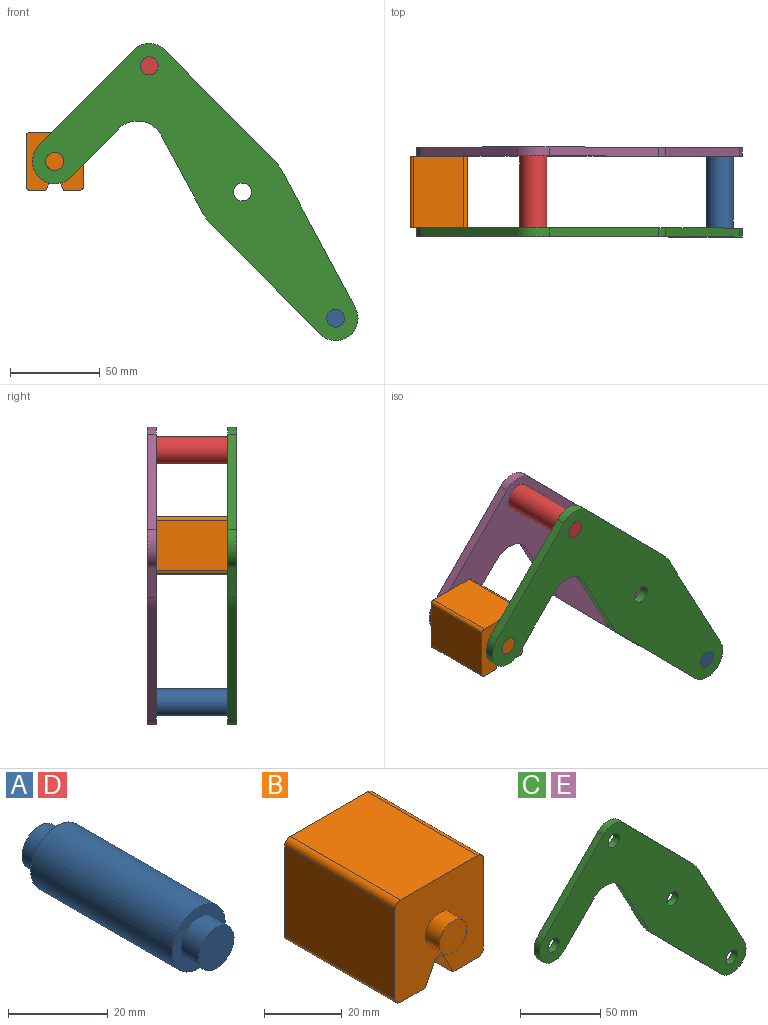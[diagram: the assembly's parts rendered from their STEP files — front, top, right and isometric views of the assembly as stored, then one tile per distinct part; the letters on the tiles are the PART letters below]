
ASSEMBLY  parts=5 mates=3
PART A: 7 faces, bbox 15x50x15 mm
  f0: cylinder r=7.5mm len=40mm, axis (0,-1,0), area 1885mm2, adj f2,f5
  f1: cylinder r=5mm len=10mm, axis (0,1,0), area 157.1mm2, adj f2,f3
  f2: plane 15x15mm, normal (0,-1,0), area 98.2mm2, adj f0,f1
  f3: plane 10x10mm, normal (0,-1,0), area 78.5mm2, adj f1
  f4: cylinder r=5mm len=10mm, axis (0,-1,0), area 157.1mm2, adj f5,f6
  f5: plane 15x15mm, normal (0,1,0), area 98.2mm2, adj f0,f4
  f6: plane 10x10mm, normal (0,1,0), area 78.5mm2, adj f4
PART B: 18 faces, bbox 32.1x50x32.1 mm
  f0: plane 40x28.08mm, normal (1,0,0), area 1123.1mm2, adj f4,f10,f13,f14
  f1: plane 40x9.04mm, normal (0,0,-1), area 361.6mm2, adj f2,f4,f10,f14
  f2: plane 40x6.42mm, normal (-0.89,0,-0.45), area 287.2mm2, adj f1,f4,f10,f15
  f3: plane 40x6.42mm, normal (0.89,0,-0.45), area 287.2mm2, adj f4,f5,f10,f15
  f4: plane 32.08x32.08mm, normal (0,-1,0), area 900.6mm2, adj f0,f1,f2,f3,f5,f6,f7,f9
  f5: plane 40x9.04mm, normal (0,0,-1), area 361.6mm2, adj f3,f4,f10,f16
  f6: plane 40x28.08mm, normal (0,0,1), area 1123.1mm2, adj f4,f10,f13,f17
  f7: plane 40x28.08mm, normal (-1,0,0), area 1123.1mm2, adj f4,f10,f16,f17
  f8: plane 10x10mm, normal (0,-1,0), area 78.5mm2, adj f9
  f9: cylinder r=5mm len=10mm, axis (0,1,0), area 157.1mm2, adj f4,f8
  f10: plane 32.08x32.08mm, normal (0,1,0), area 900.6mm2, adj f0,f1,f2,f3,f5,f6,f7,f12
  f11: plane 10x10mm, normal (0,1,0), area 78.5mm2, adj f12
  f12: cylinder r=5mm len=10mm, axis (0,-1,0), area 157.1mm2, adj f10,f11
  f13: cylinder r=2mm len=40mm, axis (0,1,0), area 125.7mm2, adj f0,f4,f6,f10
  f14: cylinder r=2mm len=40mm, axis (0,-1,0), area 125.7mm2, adj f0,f1,f4,f10
  f15: cylinder r=2mm len=40mm, axis (0,1,0), area 177.1mm2, adj f2,f3,f4,f10
  f16: cylinder r=2mm len=40mm, axis (0,1,0), area 125.7mm2, adj f4,f5,f7,f10
  f17: cylinder r=2mm len=40mm, axis (0,-1,0), area 125.7mm2, adj f4,f6,f7,f10
PART C: 18 faces, bbox 181.7x5x165.8 mm
  f0: plane 43.49x23.35mm, normal (-0.88,0,-0.47), area 246.8mm2, adj f1,f14,f16,f17
  f1: cylinder r=25mm len=5.75mm, axis (0,1,0), area 35.8mm2, adj f0,f2,f16,f17
  f2: plane 61.6x60.87mm, normal (-0.71,0,-0.7), area 433mm2, adj f1,f3,f16,f17
  f3: cylinder r=12.5mm len=21.39mm, axis (0,1,0), area 178.4mm2, adj f2,f4,f16,f17
  f4: plane 76.3x40.96mm, normal (0.88,0,0.47), area 433mm2, adj f3,f5,f16,f17
  f5: cylinder r=25mm len=5.75mm, axis (0,1,0), area 35.8mm2, adj f4,f6,f16,f17
  f6: plane 61.6x60.87mm, normal (0.71,0,0.7), area 433mm2, adj f5,f7,f16,f17
  f7: cylinder r=12.5mm len=17.78mm, axis (0,1,0), area 98.9mm2, adj f6,f8,f16,f17
  f8: plane 53.35x52.71mm, normal (-0.71,0,0.7), area 375mm2, adj f7,f9,f16,f17
  f9: cylinder r=12.5mm len=21.39mm, axis (0,1,0), area 196.3mm2, adj f8,f10,f16,f17
  f10: plane 26.86x26.54mm, normal (0.71,0,-0.7), area 188.8mm2, adj f9,f14,f16,f17
  f11: cylinder r=5mm len=10mm, axis (0,1,0), area 157.1mm2, adj f16,f17
  f12: cylinder r=5mm len=10mm, axis (0,1,0), area 157.1mm2, adj f16,f17
  f13: cylinder r=5mm len=10mm, axis (0,1,0), area 157.1mm2, adj f16,f17
  f14: cylinder r=15mm len=23.89mm, axis (0,1,0), area 140.2mm2, adj f0,f10,f16,f17
  f15: cylinder r=5mm len=10mm, axis (0,1,0), area 157.1mm2, adj f16,f17
  f16: plane 181.66x165.78mm, normal (0,-1,0), area 8710.1mm2, adj f0,f1,f2,f3,f4,f5,f6,f7
  f17: plane 181.66x165.78mm, normal (0,1,0), area 8710.1mm2, adj f0,f1,f2,f3,f4,f5,f6,f7
PART D: same geometry as A
PART E: same geometry as C
PLACE A t=(98.81,-19.47,-146.2)mm
PLACE B t=(-5.15,-19.47,-5.42)mm
PLACE C t=(-5.15,-19.47,-5.42)mm fixed
PLACE D t=(-5.15,-19.47,-5.42)mm
PLACE E t=(-5.15,25.53,-5.42)mm
MATE fastened E.f7 <-> D.f0  axis (0,-1,0) through (-57.12,20.53,64.97)mm
MATE fastened A.f0 <-> C.f3  axis (0,-1,0) through (46.83,-19.47,-75.81)mm
MATE revolute B.f9 <-> C.f9  axis (0,-1,0) through (-109.83,-19.47,11.62)mm
